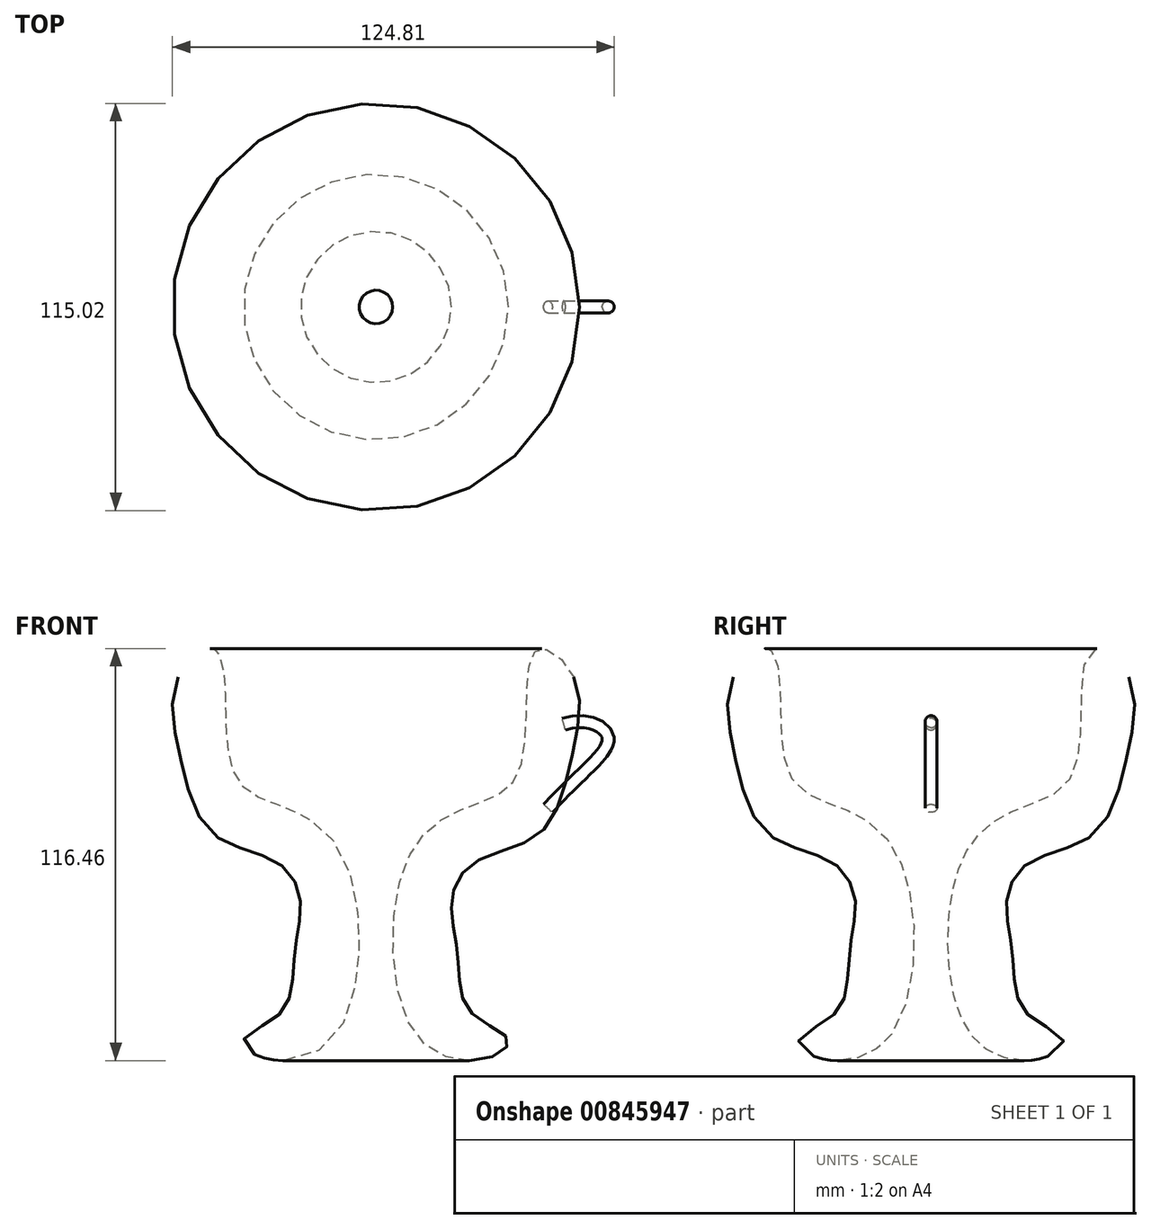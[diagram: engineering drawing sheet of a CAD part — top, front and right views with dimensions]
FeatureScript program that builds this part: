
annotation { "Feature Type Name" : "Feature", "Feature Type Description" : "" }
export const myFeature = defineFeature(function(context is Context, id is Id, definition is map)
    precondition{}
    {
        {
            var Q0;
            Q0=qCreatedBy(makeId("Front.planeOp"),FACE);
            var sketch = newSketch(context, id + "F0", { "sketchPlane" : qUnion([Q0])});
            skFitSpline(sketch, "E0", {"points": [v(55.89, 52.33) * mm, v(55.24, 29.3) * mm, v(45.98, 7.97) * mm, v(27.9, 0) * mm, v(21.43, -10.34) * mm, v(22.5, -21.75) * mm, v(23.58, -33.17) * mm, v(27.46, -43.07) * mm, v(37.37, -50.18) * mm, v(32.2, -55.13) * mm, v(11.74, -49.32) * mm, v(7.86, -1.72) * mm, v(23.58, 14.65) * mm, v(38.66, 22.61) * mm, v(42.54, 45.01) * mm, v(45.98, 60.3) * mm, v(55.89, 52.33) * mm]});
            skLineSegment(sketch, "E1", {"start": v(0, 75.6) * mm, "end": v(0, -74.73) * mm});
            skSolve(sketch);
        }
        {
            var Q0;
            Q0=makeQuery(id+"F0.imprint","IMPRINT",FACE,{"disambiguationData":[TD([[makeQuery(id+"F0.imprint","IMPRINT",EDGE,{"derivedFrom":sQuery(id+"F0.wireOp",EDGE,"E0")}),-1.0]])]});
            var Q1;
            Q1=sQuery(id+"F0.wireOp",EDGE,"E1");
            revolve(context, id + "F1", {"surfaceOperationType" : NewSurfaceOperationType.NEW, "entities" : qUnion([Q0]), "axis" : qUnion([Q1]), "revolveType" : RevolveType.FULL});
        }
        {
            var Q0;
            Q0=qCreatedBy(makeId("Front.planeOp"),FACE);
            var sketch = newSketch(context, id + "F2", { "sketchPlane" : qUnion([Q0])});
            skFitSpline(sketch, "E2", {"points": [v(53.09, 38.98) * mm, v(65.46, 35.46) * mm, v(48.57, 15.3) * mm], "startDerivative": vector(50.67, 14.5) * mm, "endDerivative": vector(-53.2, -57.37) * mm});
            skSolve(sketch);
        }
        {
            var Q0;
            Q0 = qBodyType(qCreatedBy(id + "F2" ,EDGE), BodyType.WIRE);
            var Q1;
            Q1=sQuery(id+"F2.wireOp",VERTEX,"E2.end");
            cPlane(context, id + "F3", {"entities" : qUnion([Q0, Q1]), "cplaneType" : CPlaneType.CURVE_POINT, "offset" : 25.4 * mm, "width" : 152.4 * mm, "height" : 152.4 * mm});
        }
        {
            var Q0;
            Q0=qCreatedBy(id+"F3.planeOp",FACE);
            var sketch = newSketch(context, id + "F4", { "sketchPlane" : qUnion([Q0])});
            skCircle(sketch, "E3", {"center": v(25.28, 0) * mm, "radius": 1.7 * mm});
            skSolve(sketch);
        }
        {
            var Q0;
            Q0=makeQuery(id+"F4.imprint","IMPRINT",FACE,{"disambiguationData":[TD([[makeQuery(id+"F4.imprint","IMPRINT",EDGE,{"derivedFrom":sQuery(id+"F4.wireOp",EDGE,"E3")}),1.0]])]});
            var Q1;
            Q1=sQuery(id+"F2.wireOp",EDGE,"E2");
            sweep(context, id + "F5", {"profiles" : qUnion([Q0]), "path" : qUnion([Q1])});
        }
    });
